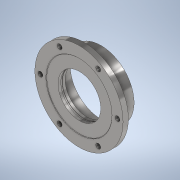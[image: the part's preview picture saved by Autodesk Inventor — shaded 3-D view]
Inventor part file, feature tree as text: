
AUTODESK INVENTOR PART (.ipt)
format: ipt  version: 2020 (Build 240168000, 168)  size: 203,264 bytes
history: native  units: mm
features: extrude x7, sketch x7, other x3, plane x2, reference x2, fillet x1, projected_geometry x1
ambient origin geometry x8: Origin, YZ Plane, XZ Plane, XY Plane, X Axis, Y Axis, Z Axis, Center Point
bodies: 实体1 (feature_tree)
feature tree (23):
  plane  "工作平面1"
  extrude  "拉伸1"  Depth=11.0mm
  extrude  "拉伸2"  Depth=12.0mm TaperAngle=0.0deg
  extrude  "拉伸3"  Depth=12.0mm
  extrude  "拉伸4"  Depth=38.0mm TaperAngle=0.0deg
  fillet  "圆角1"  Radius=150.0mm
  extrude  "拉伸5"  Depth=1.0mm
  plane  "工作平面2"
  extrude  "拉伸6"  Depth=5.0mm TaperAngle=0.0deg
  extrude  "拉伸7"  Depth=3.55mm TaperAngle=0.0deg
  sketch  "草图1"  dims[d0=175.0mm d1=11.0mm]
  reference  "参考1"
  sketch  "草图2"  dims[d2=60.0mm d4=360.0deg d6=12.0mm d7=0.0mm]
  reference  "参考2"
  sketch  "草图3"  dims[d9=12.0mm d10=0.0mm d11=150.0mm]
  sketch  "草图4"  dims[d12=140.0mm d13=38.0mm d14=0.0mm d15=150.0mm]
  sketch  "草图5"  dims[d16=1.0mm d17=0.0mm d18=1.0mm]
  projected_geometry  "投影回路1"
  sketch  "草图6"  dims[d19=97.0mm d20=5.0mm d21=0.0mm]
  sketch  "草图7"  dims[d22=98.55mm d23=3.55mm d24=0.0mm d25=1.0mm d26=2.0mm d27=0.0mm]
  other  "<userpath>\Desktop\ME_course_project\课设试试\shaft_try_1.iam"
  other  "shaft_try_1.iam"
  other  "xia(1):1"
